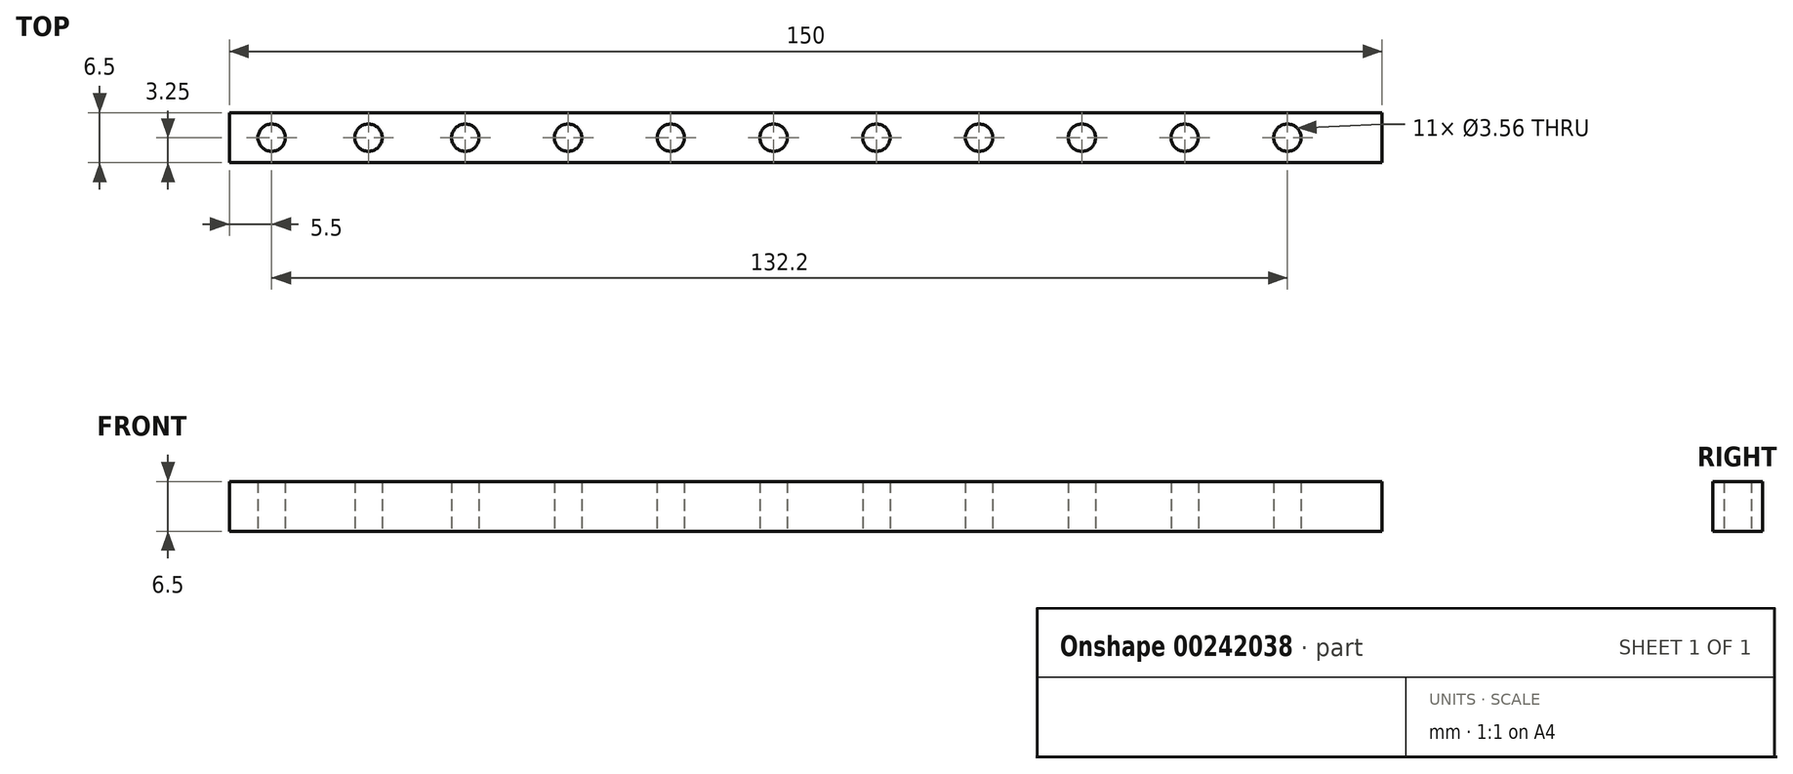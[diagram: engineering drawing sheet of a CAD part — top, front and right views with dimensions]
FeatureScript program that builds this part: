
annotation { "Feature Type Name" : "Feature", "Feature Type Description" : "" }
export const myFeature = defineFeature(function(context is Context, id is Id, definition is map)
    precondition{}
    {
        {
            var Q0;
            Q0=qCreatedBy(makeId("Top.planeOp"),FACE);
            var sketch = newSketch(context, id + "F0", { "sketchPlane" : qUnion([Q0])});
            skLineSegment(sketch, "E0.bottom", {"start": v(0, 0) * mm, "end": v(150, 0) * mm});
            skLineSegment(sketch, "E0.top", {"start": v(0, 6.5) * mm, "end": v(150, 6.5) * mm});
            skLineSegment(sketch, "E0.left", {"start": v(0, 0) * mm, "end": v(0, 6.5) * mm});
            skLineSegment(sketch, "E0.right", {"start": v(150, 0) * mm, "end": v(150, 6.5) * mm});
            skCircle(sketch, "E1", {"center": v(5.5, 3.25) * mm, "radius": 1.78 * mm});
            skPoint(sketch, "E1.centerSnap0", {"position": v(0, 3.25) * mm});
            skCircle(sketch, "E2.1.0.0", {"center": v(18.1, 3.25) * mm, "radius": 1.78 * mm});
            skLineSegment(sketch, "E2.direction1", {"start": v(5.5, 3.25) * mm, "end": v(18.1, 3.25) * mm, "construction": true});
            skCircle(sketch, "E3.0.2.0", {"center": v(30.7, 3.25) * mm, "radius": 1.78 * mm});
            skCircle(sketch, "E4.1.0.0", {"center": v(44.07, 3.25) * mm, "radius": 1.78 * mm});
            skCircle(sketch, "E4.2.0.0", {"center": v(57.45, 3.25) * mm, "radius": 1.78 * mm});
            skCircle(sketch, "E4.3.0.0", {"center": v(70.83, 3.25) * mm, "radius": 1.78 * mm});
            skCircle(sketch, "E4.4.0.0", {"center": v(84.2, 3.25) * mm, "radius": 1.78 * mm});
            skLineSegment(sketch, "E4.direction1", {"start": v(30.7, 3.25) * mm, "end": v(44.07, 3.25) * mm, "construction": true});
            skCircle(sketch, "E5.0.5.0", {"center": v(97.57, 3.25) * mm, "radius": 1.78 * mm});
            skCircle(sketch, "E5.0.6.0", {"center": v(110.95, 3.25) * mm, "radius": 1.78 * mm});
            skCircle(sketch, "E5.0.7.0", {"center": v(124.32, 3.25) * mm, "radius": 1.78 * mm});
            skCircle(sketch, "E5.0.8.0", {"center": v(137.7, 3.25) * mm, "radius": 1.78 * mm});
            skSolve(sketch);
        }
        {
            var Q0;
            Q0 = qSketchRegion(id + "F0", true);
            extrude(context, id + "F1", {"entities" : qUnion([Q0]), "depth" : 6.5 * mm});
        }
    });
